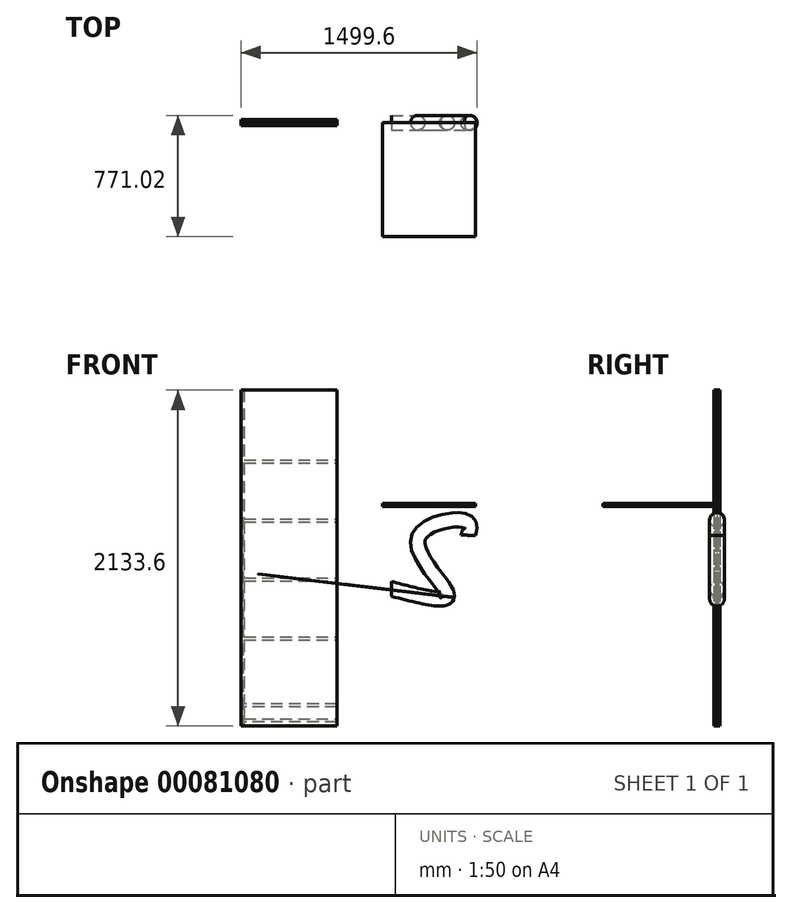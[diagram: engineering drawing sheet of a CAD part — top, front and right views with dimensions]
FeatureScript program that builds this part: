
annotation { "Feature Type Name" : "Feature", "Feature Type Description" : "" }
export const myFeature = defineFeature(function(context is Context, id is Id, definition is map)
    precondition{}
    {
        {
            var Q0;
            Q0=qCreatedBy(makeId("Front.planeOp"),FACE);
            var sketch = newSketch(context, id + "F0", { "sketchPlane" : qUnion([Q0])});
            skLineSegment(sketch, "E0.bottom", {"start": v(-345.06, 769.9) * mm, "end": v(-954.66, 769.9) * mm});
            skLineSegment(sketch, "E0.top", {"start": v(-345.06, -1363.7) * mm, "end": v(-954.66, -1363.7) * mm});
            skLineSegment(sketch, "E1", {"start": v(-941.96, 769.9) * mm, "end": v(-941.96, -1363.7) * mm});
            skLineSegment(sketch, "E2", {"start": v(-935.6, 769.9) * mm, "end": v(-935.6, 325.4) * mm});
            skLineSegment(sketch, "E3", {"start": v(-345.06, -1338.3) * mm, "end": v(-935.6, -1338.3) * mm});
            skLineSegment(sketch, "E4.trimOffspring", {"start": v(-935.6, -1319.24) * mm, "end": v(-345.06, -1319.24) * mm});
            skLineSegment(sketch, "E5", {"start": v(-954.66, 769.9) * mm, "end": v(-954.66, -1363.7) * mm});
            skLineSegment(sketch, "E6", {"start": v(-345.06, -1243.04) * mm, "end": v(-935.6, -1243.04) * mm});
            skLineSegment(sketch, "E7", {"start": v(-345.06, -1224) * mm, "end": v(-935.6, -1224) * mm});
            skLineSegment(sketch, "E8.trimOffspring", {"start": v(-935.6, -1243.04) * mm, "end": v(-935.6, -1319.24) * mm});
            skLineSegment(sketch, "E9.trimOffspring", {"start": v(-935.6, -1338.3) * mm, "end": v(-935.6, -1363.7) * mm});
            skLineSegment(sketch, "E10.bottom", {"start": v(-935.6, -68.3) * mm, "end": v(-345.06, -68.3) * mm});
            skLineSegment(sketch, "E10.top", {"start": v(-935.6, -817.6) * mm, "end": v(-345.06, -817.6) * mm});
            skLineSegment(sketch, "E10.left", {"start": v(-935.6, -68.3) * mm, "end": v(-935.6, -423.9) * mm});
            skLineSegment(sketch, "E11.bottom", {"start": v(-935.6, -49.24) * mm, "end": v(-345.06, -49.24) * mm});
            skLineSegment(sketch, "E11.top", {"start": v(-935.6, -798.54) * mm, "end": v(-345.06, -798.54) * mm});
            skLineSegment(sketch, "E12.bottom", {"start": v(-935.6, -423.9) * mm, "end": v(-345.06, -423.9) * mm});
            skLineSegment(sketch, "E12.top", {"start": v(-935.6, -442.94) * mm, "end": v(-345.06, -442.94) * mm});
            skLineSegment(sketch, "E13.bottom", {"start": v(-935.6, 325.4) * mm, "end": v(-345.06, 325.4) * mm});
            skLineSegment(sketch, "E13.top", {"start": v(-935.6, 306.36) * mm, "end": v(-345.06, 306.36) * mm});
            skLineSegment(sketch, "E14.trimOffspring", {"start": v(-345.06, 306.36) * mm, "end": v(-345.06, -1363.7) * mm});
            skLineSegment(sketch, "E15", {"start": v(-345.06, 769.9) * mm, "end": v(-345.06, 325.4) * mm});
            skLineSegment(sketch, "E16.trimOffspring", {"start": v(-935.6, 306.36) * mm, "end": v(-935.6, -49.24) * mm});
            skLineSegment(sketch, "E17.trimOffspring", {"start": v(-935.6, -442.94) * mm, "end": v(-935.6, -798.54) * mm});
            skLineSegment(sketch, "E18.trimOffspring", {"start": v(-935.6, -817.6) * mm, "end": v(-935.6, -1224) * mm});
            skLineSegment(sketch, "E19", {"start": v(-345.06, 306.36) * mm, "end": v(-345.06, 325.4) * mm});
            skSolve(sketch);
        }
        {
            var Q0;
            Q0 = qSketchRegion(id + "F0", true);
            extrude(context, id + "F1", {"entities" : qUnion([Q0]), "oppositeDirection" : true, "depth" : 19.05 * mm});
        }
        {
            var Q0;
            {var subQ12=sQuery(id+"F0.wireOp",EDGE,"E1");Q0=makeQuery(id+"F0.imprint","IMPRINT",FACE,{"disambiguationData":[TD([[makeQuery(id+"F0.imprint","IMPRINT",EDGE,{"derivedFrom":subQ12}),1.0]])]});}
            extrude(context, id + "F2", {"entities" : qUnion([Q0]), "operationType" : NewBodyOperationType.REMOVE, "oppositeDirection" : true, "depth" : 9.52 * mm});
        }
        {
            var Q0;
            Q0=qCreatedBy(makeId("Front.planeOp"),FACE);
            var sketch = newSketch(context, id + "F3", { "sketchPlane" : qUnion([Q0])});
            skLineSegment(sketch, "E20.bottom", {"start": v(-57.45, 49.24) * mm, "end": v(533.1, 49.24) * mm});
            skLineSegment(sketch, "E20.top", {"start": v(-57.45, 30.2) * mm, "end": v(533.1, 30.2) * mm});
            skLineSegment(sketch, "E20.left", {"start": v(-57.45, 49.24) * mm, "end": v(-57.45, 30.2) * mm});
            skLineSegment(sketch, "E20.right", {"start": v(533.1, 49.24) * mm, "end": v(533.1, 30.2) * mm});
            skSolve(sketch);
        }
        {
            var Q0;
            Q0 = qSketchRegion(id + "F3", true);
            extrude(context, id + "F4", {"entities" : qUnion([Q0]), "depth" : 723.9 * mm});
        }
        {
            var Q0;
            Q0 = qSketchRegion(id + "F0", true);
            extrude(context, id + "F9", {"entities" : qUnion([Q0]), "depth" : 19.05 * mm});
        }
        {
            var Q0;
            {var subQ12=sQuery(id+"F0.wireOp",EDGE,"E1");Q0=makeQuery(id+"F0.imprint","IMPRINT",FACE,{"disambiguationData":[TD([[makeQuery(id+"F0.imprint","IMPRINT",EDGE,{"derivedFrom":subQ12}),1.0]])]});}
            extrude(context, id + "F5", {"entities" : qUnion([Q0]), "operationType" : NewBodyOperationType.REMOVE, "depth" : 9.52 * mm});
        }
        {
            var Q0;
            Q0=qCreatedBy(makeId("Front.planeOp"),FACE);
            var sketch = newSketch(context, id + "F6", { "sketchPlane" : qUnion([Q0])});
            skFitSpline(sketch, "E21", {"points": [v(0, -496.08) * mm, v(359.47, -531.25) * mm, v(174.83, -175.16) * mm, v(473.77, -67.45) * mm, v(484.76, -150.98) * mm], "startDerivative": vector(1892.24, -496.41) * mm, "endDerivative": vector(-214.3, -734.47) * mm});
            skSolve(sketch);
        }
        {
            var Q0;
            Q0=qCreatedBy(makeId("Right.planeOp"),FACE);
            var sketch = newSketch(context, id + "F7", { "sketchPlane" : qUnion([Q0])});
            skCircle(sketch, "E22", {"center": v(0, -491.8) * mm, "radius": 47.12 * mm});
            skSolve(sketch);
        }
        {
            var Q0;
            Q0=makeQuery(id+"F7.imprint","IMPRINT",FACE,{"disambiguationData":[TD([[makeQuery(id+"F7.imprint","IMPRINT",EDGE,{"derivedFrom":sQuery(id+"F7.wireOp",EDGE,"E22")}),1.0]])]});
            var Q1;
            Q1=sQuery(id+"F6.wireOp",EDGE,"E21");
            sweep(context, id + "F8", {"profiles" : qUnion([Q0]), "path" : qUnion([Q1])});
        }
    });
